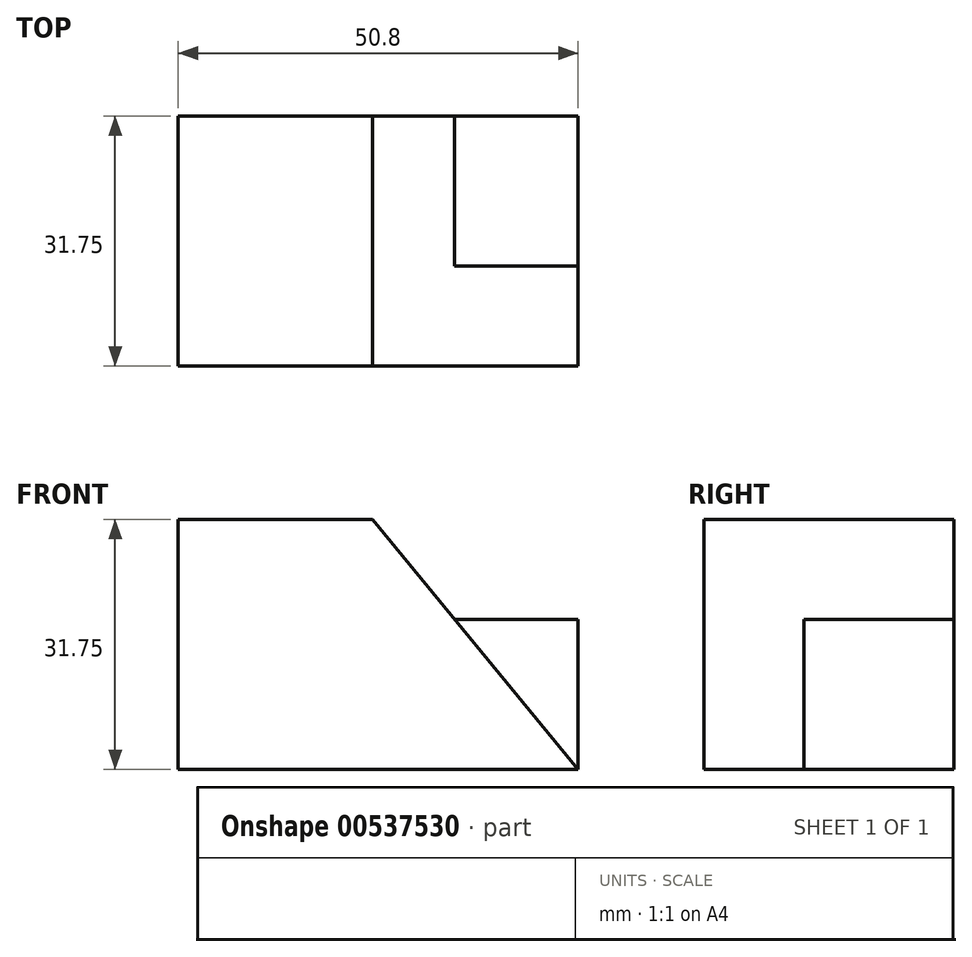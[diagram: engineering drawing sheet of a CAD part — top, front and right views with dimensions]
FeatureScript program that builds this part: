
annotation { "Feature Type Name" : "Feature", "Feature Type Description" : "" }
export const myFeature = defineFeature(function(context is Context, id is Id, definition is map)
    precondition{}
    {
        {
            var Q0;
            Q0=qCreatedBy(makeId("Front.planeOp"),FACE);
            var sketch = newSketch(context, id + "F0", { "sketchPlane" : qUnion([Q0])});
            skLineSegment(sketch, "E0", {"start": v(0, 0) * mm, "end": v(50.8, 0) * mm});
            skLineSegment(sketch, "E1", {"start": v(50.8, 0) * mm, "end": v(50.8, 31.75) * mm});
            skLineSegment(sketch, "E2", {"start": v(50.8, 31.75) * mm, "end": v(0, 31.75) * mm});
            skLineSegment(sketch, "E3", {"start": v(0, 31.75) * mm, "end": v(0, 0) * mm});
            skSolve(sketch);
        }
        {
            var Q0;
            Q0=makeQuery(id+"F0.imprint","IMPRINT",FACE,{"disambiguationData":[TD([[makeQuery(id+"F0.imprint","IMPRINT",EDGE,{"derivedFrom":sQuery(id+"F0.wireOp",EDGE,"E0")}),1.0]])]});
            extrude(context, id + "F1", {"entities" : qUnion([Q0]), "depth" : 31.75 * mm, "offsetDistance" : 25.4 * mm});
        }
        {
            var Q0;
            Q0=makeQuery(id+"F1.opExtrude","CAP_FACE",FACE,{"disambiguationData":[OSD([sQuery(id+"F0.wireOp",EDGE,"E0"),sQuery(id+"F0.wireOp",EDGE,"E1"),sQuery(id+"F0.wireOp",EDGE,"E2"),sQuery(id+"F0.wireOp",EDGE,"E3")])],"isStart":false});
            var sketch = newSketch(context, id + "F2", { "sketchPlane" : qUnion([Q0])});
            skLineSegment(sketch, "E4", {"start": v(24.67, 31.75) * mm, "end": v(50.8, 0) * mm});
            skSolve(sketch);
        }
        {
            var Q0;
            {var subQ0=sQuery(id+"F2.wireOp",EDGE,"E4");Q0=makeQuery(id+"F2.imprint","IMPRINT",FACE,{"disambiguationData":[TD([[makeQuery(id+"F2.imprint","IMPRINT",EDGE,{"derivedFrom":subQ0}),1.0]])]});}
            extrude(context, id + "F3", {"entities" : qUnion([Q0]), "operationType" : NewBodyOperationType.REMOVE, "oppositeDirection" : true, "depth" : 12.7 * mm, "offsetDistance" : 25.4 * mm});
        }
        {
            var Q0;
            Q0=makeQuery(id+"F3.boolean.opBoolean","COPY",FACE,{"derivedFrom":makeQuery(id+"F3.opExtrude","CAP_FACE",FACE,{"disambiguationData":[OSD([sQuery(id+"F0.wireOp",EDGE,"E1"),sQuery(id+"F0.wireOp",EDGE,"E2"),sQuery(id+"F2.wireOp",EDGE,"E4")])],"isStart":false})});
            var sketch = newSketch(context, id + "F4", { "sketchPlane" : qUnion([Q0])});
            skLineSegment(sketch, "E5", {"start": v(35.12, 19.05) * mm, "end": v(50.8, 19.05) * mm});
            skSolve(sketch);
        }
        {
            var Q0;
            {var subQ0=sQuery(id+"F4.wireOp",EDGE,"E5");Q0=makeQuery(id+"F4.imprint","IMPRINT",FACE,{"disambiguationData":[TD([[makeQuery(id+"F4.imprint","IMPRINT",EDGE,{"derivedFrom":subQ0}),1.0]])]});}
            extrude(context, id + "F5", {"entities" : qUnion([Q0]), "operationType" : NewBodyOperationType.REMOVE, "oppositeDirection" : true, "depth" : 19.05 * mm, "offsetDistance" : 25.4 * mm});
        }
    });
